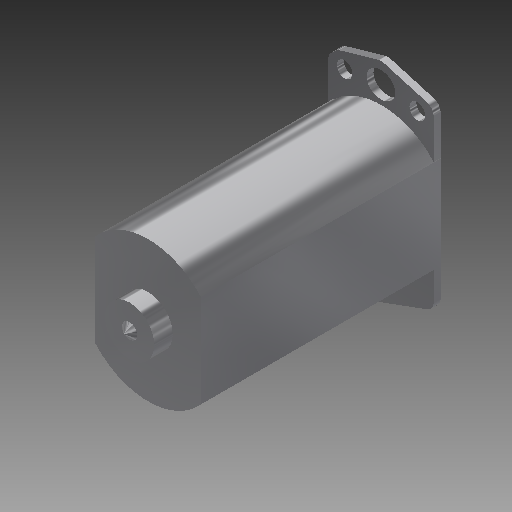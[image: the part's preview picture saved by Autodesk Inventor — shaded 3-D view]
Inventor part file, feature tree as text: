
AUTODESK INVENTOR PART (.ipt)
format: ipt  version: 2018 (Build 220112000, 112)  size: 150,528 bytes
history: native  units: in
note: dims shown in document units (in); Inventor stores cm internally (conversion verified against a paired STEP export)
features: other x2, imported_body x2, fillet x1
ambient origin geometry x8: Origin, YZ Plane, XZ Plane, XY Plane, X Axis, Y Axis, Z Axis, Center Point
bodies: Body1 (feature_tree), Body2 (feature_tree)
feature tree (5):
  fillet  "Fillet1"  [1 undecoded]
  other  "AM-2235 motor.ipt1"
  other  "Boss-Extrude4"
  imported_body  "Base1"
  imported_body  "Base2"
note: 1 required parameter value undecoded (feature->parameter linkage not recoverable at this tier; creation-order binding heuristic only, values carry confidence <= 0.55)
